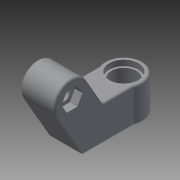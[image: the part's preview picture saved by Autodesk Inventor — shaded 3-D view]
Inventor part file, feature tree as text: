
AUTODESK INVENTOR PART (.ipt)
format: ipt  version: 2013 (Build 170138000, 138)  size: 164,864 bytes
history: native  units: mm
features: extrude x8, sketch x8, chamfer x1
ambient origin geometry x8: Origin, YZ Plane, XZ Plane, XY Plane, X Axis, Y Axis, Z Axis, Center Point
bodies: Solid1 (feature_tree)
feature tree (17):
  extrude  "Extrusion1"  Depth=50.0mm
  extrude  "Extrusion2"  Depth=25.0mm
  extrude  "Extrusion13"  Depth=25.0mm TaperAngle=0.0deg
  extrude  "Extrusion14"  TaperAngle=120.0deg  [1 undecoded]
  extrude  "Extrusion15"  Depth=6.0mm TaperAngle=0.0deg
  chamfer  "Chamfer4"  Distance=4.0mm
  extrude  "Extrusion16"  Depth=4.0mm TaperAngle=0.0deg
  extrude  "Extrusion17"  Depth=3.0mm
  extrude  "Extrusion18"  Depth=10.0mm TaperAngle=0.0deg
  sketch  "Sketch1"  dims[d0=8.1mm d2=50.0mm]
  sketch  "Sketch2"  dims[d3=14.0mm d4=25.0mm]
  sketch  "Sketch13"  dims[d6=25.0mm d7=25.0mm d8=0.0mm]
  sketch  "Sketch14"  dims[d9=25.0mm d10=0.0mm d40=120.0deg]
  sketch  "Sketch15"  dims[d59=18.1mm d61=6.0mm d62=0.0mm]
  sketch  "Sketch16"  dims[d63=21.1mm d65=4.0mm d66=0.0mm]
  sketch  "Sketch17"  dims[d67=21.1mm d69=4.0mm d70=0.0mm]
  sketch  "Sketch18"  dims[d72=1.5mm d73=2.0mm d74=45.0deg d76=3.0mm d77=10.0mm d78=0.0mm d80=13.2mm d81=5.5mm d82=0.0mm d83=17.0mm d85=5.5mm d86=0.0mm]
note: 1 required parameter value undecoded (feature->parameter linkage not recoverable at this tier; creation-order binding heuristic only, values carry confidence <= 0.55)
